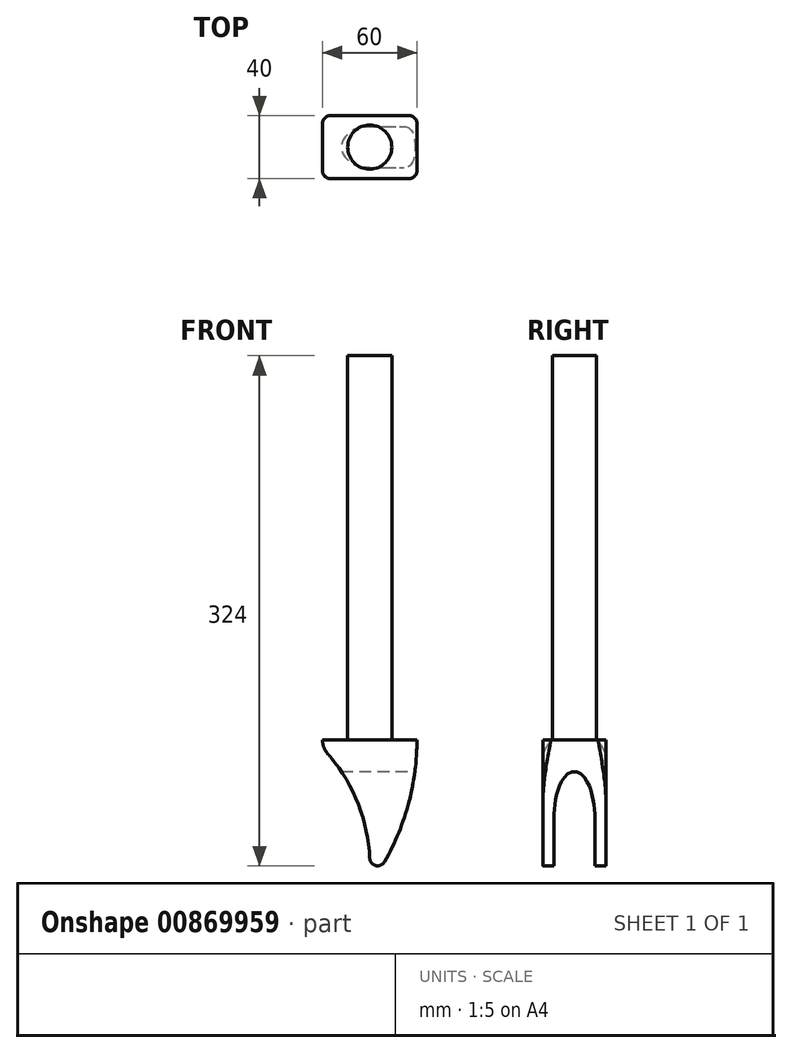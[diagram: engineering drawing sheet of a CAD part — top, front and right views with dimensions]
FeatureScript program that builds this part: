
annotation { "Feature Type Name" : "Feature", "Feature Type Description" : "" }
export const myFeature = defineFeature(function(context is Context, id is Id, definition is map)
    precondition{}
    {
        {
            var Q0;
            Q0=qCreatedBy(makeId("Top.planeOp"),FACE);
            var sketch = newSketch(context, id + "F0", { "sketchPlane" : qUnion([Q0])});
            skCircle(sketch, "E0", {"center": v(0, 0) * mm, "radius": 14 * mm});
            skSolve(sketch);
        }
        {
            var Q0;
            Q0=makeQuery(id+"F0.imprint","IMPRINT",FACE,{"disambiguationData":[TD([[makeQuery(id+"F0.imprint","IMPRINT",EDGE,{"derivedFrom":sQuery(id+"F0.wireOp",EDGE,"E0")}),1.0]])]});
            extrude(context, id + "F1", {"entities" : qUnion([Q0]), "depth" : 244 * mm, "offsetDistance" : 25 * mm});
        }
        {
            var Q0;
            Q0=qCreatedBy(makeId("Top.planeOp"),FACE);
            var sketch = newSketch(context, id + "F2", { "sketchPlane" : qUnion([Q0])});
            skLineSegment(sketch, "E1.bottom", {"start": v(30, 20) * mm, "end": v(-30, 20) * mm});
            skLineSegment(sketch, "E1.top", {"start": v(30, -20) * mm, "end": v(-30, -20) * mm});
            skLineSegment(sketch, "E1.left", {"start": v(30, 20) * mm, "end": v(30, -20) * mm});
            skLineSegment(sketch, "E1.right", {"start": v(-30, 20) * mm, "end": v(-30, -20) * mm});
            skPoint(sketch, "E1.middle", {"position": v(0, 0) * mm});
            skSolve(sketch);
        }
        {
            var Q0;
            Q0=makeQuery(id+"F2.imprint","IMPRINT",FACE,{"disambiguationData":[TD([[makeQuery(id+"F2.imprint","IMPRINT",EDGE,{"derivedFrom":sQuery(id+"F2.wireOp",EDGE,"E1.bottom")}),1.0]])]});
            extrude(context, id + "F3", {"entities" : qUnion([Q0]), "operationType" : NewBodyOperationType.ADD, "oppositeDirection" : true, "depth" : 80 * mm, "offsetDistance" : 25 * mm});
        }
        {
            var Q0;
            Q0=makeQuery(id+"F3.opExtrude","SWEPT_EDGE",EDGE,{"disambiguationData":[OSD([sQuery(id+"F2.wireOp",EDGE,"E1.top"),sQuery(id+"F2.wireOp",EDGE,"E1.left")])]});
            var Q1;
            Q1=makeQuery(id+"F3.opExtrude","SWEPT_EDGE",EDGE,{"disambiguationData":[OSD([sQuery(id+"F2.wireOp",EDGE,"E1.top"),sQuery(id+"F2.wireOp",EDGE,"E1.right")])]});
            var Q2;
            Q2=makeQuery(id+"F3.opExtrude","SWEPT_EDGE",EDGE,{"disambiguationData":[OSD([sQuery(id+"F2.wireOp",EDGE,"E1.bottom"),sQuery(id+"F2.wireOp",EDGE,"E1.left")])]});
            var Q3;
            Q3=makeQuery(id+"F3.opExtrude","SWEPT_EDGE",EDGE,{"disambiguationData":[OSD([sQuery(id+"F2.wireOp",EDGE,"E1.bottom"),sQuery(id+"F2.wireOp",EDGE,"E1.right")])]});
            fillet(context, id + "F4", {"entities" : qUnion([Q0, Q1, Q2, Q3]), "radius" : 5 * mm, "tangentPropagation" : true, "allowEdgeOverflow" : false});
        }
        {
            var Q0;
            Q0=qCreatedBy(makeId("Front.planeOp"),FACE);
            var sketch = newSketch(context, id + "F5", { "sketchPlane" : qUnion([Q0])});
            skLineSegment(sketch, "E2.0", {"start": v(-30, -90) * mm, "end": v(-30, 0) * mm});
            skLineSegment(sketch, "E3.0", {"start": v(30, 0) * mm, "end": v(30, -90) * mm});
            skArc(sketch, "E4", {"start": v(-30, 0) * mm, "mid": v(-29.15, -4.7) * mm, "end": v(-26.7, -8.79) * mm});
            skArc(sketch, "E5", {"start": v(0, -75.22) * mm, "mid": v(-7.68, -39.73) * mm, "end": v(-26.7, -8.79) * mm});
            skArc(sketch, "E6", {"start": v(9.34, -77.49) * mm, "mid": v(24.75, -40.1) * mm, "end": v(30, 0) * mm});
            skArc(sketch, "E7", {"start": v(0, -75.22) * mm, "mid": v(3.82, -79.86) * mm, "end": v(9.34, -77.49) * mm});
            skLineSegment(sketch, "E8.0", {"start": v(30, -90) * mm, "end": v(-30, -90) * mm});
            skSolve(sketch);
        }
        {
            var Q0;
            Q0 = qSketchRegion(id + "F5", true);
            extrude(context, id + "F6", {"entities" : qUnion([Q0]), "operationType" : NewBodyOperationType.REMOVE, "endBound" : BoundingType.SYMMETRIC, "oppositeDirection" : true, "depth" : 80 * mm, "offsetDistance" : 25 * mm});
        }
        {
            var Q0;
            Q0=qCreatedBy(makeId("Right.planeOp"),FACE);
            var sketch = newSketch(context, id + "F7", { "sketchPlane" : qUnion([Q0])});
            skEllipticalArc(sketch, "E9", {});
            skLineSegment(sketch, "E10", {"start": v(13, -50) * mm, "end": v(13, -80) * mm});
            skLineSegment(sketch, "E11", {"start": v(-13, -50) * mm, "end": v(-13, -80) * mm});
            skLineSegment(sketch, "E12", {"start": v(-13, -80) * mm, "end": v(13, -80) * mm});
            skPoint(sketch, "E13", {"position": v(0, -20) * mm});
            const initialGuessF7  = {"E9": [0, -0.05, 0, -1, 0.03, 0.013, 1.5707963267948968, 4.71238898038469]};
            skSetInitialGuess(sketch, initialGuessF7);
            skSolve(sketch);
        }
        {
            var Q0;
            Q0 = qSketchRegion(id + "F7", true);
            extrude(context, id + "F8", {"entities" : qUnion([Q0]), "operationType" : NewBodyOperationType.REMOVE, "endBound" : BoundingType.SYMMETRIC, "oppositeDirection" : true, "depth" : 70 * mm, "offsetDistance" : 25 * mm});
        }
    });
